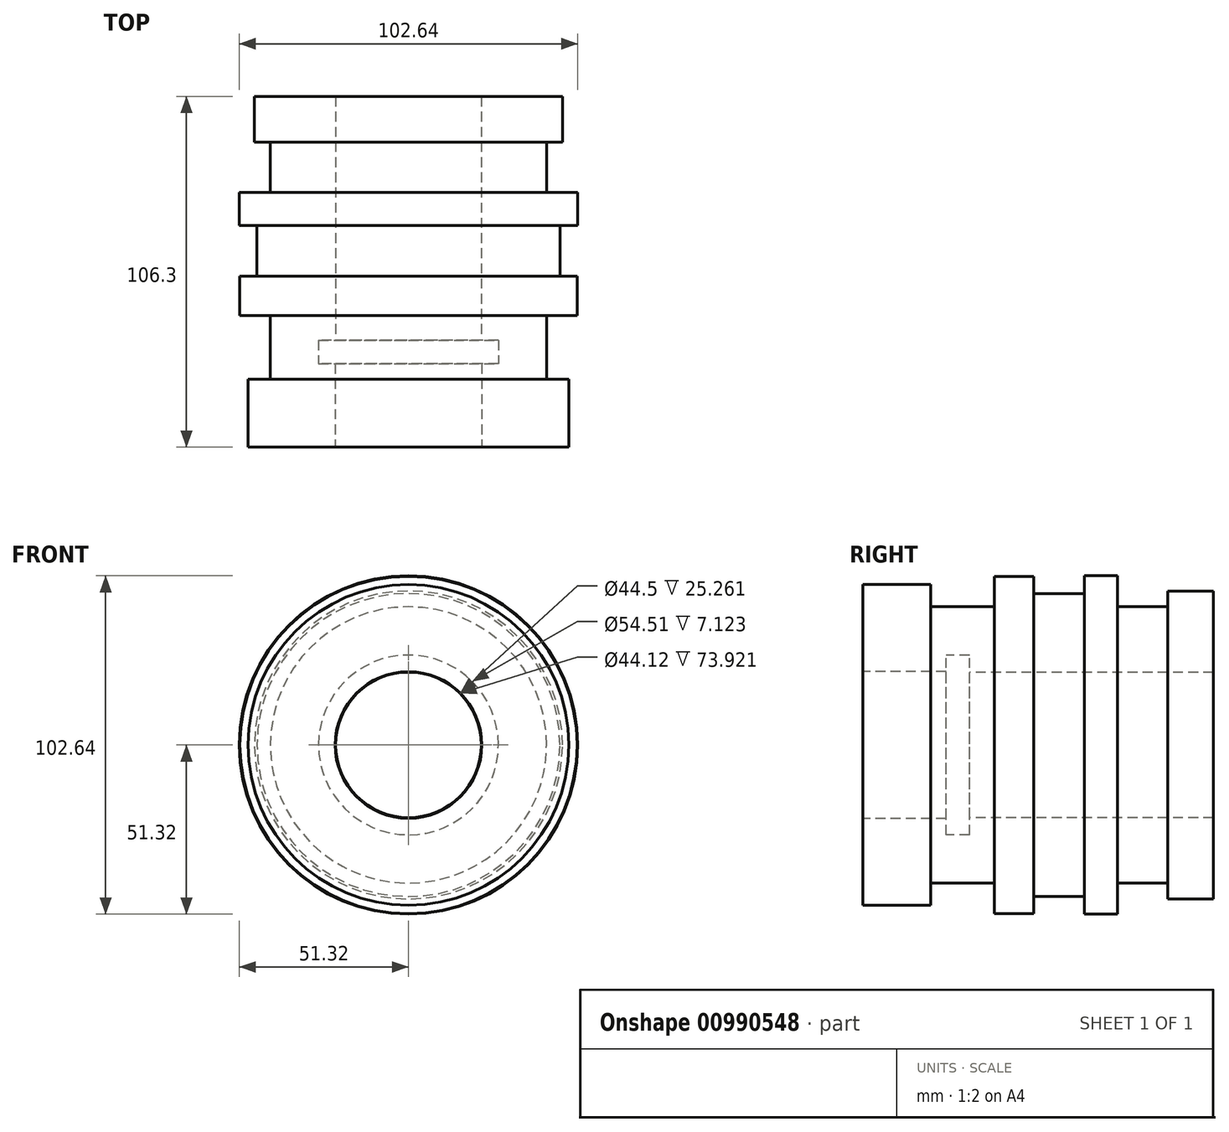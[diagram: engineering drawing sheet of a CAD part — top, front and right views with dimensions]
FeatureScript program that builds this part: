
annotation { "Feature Type Name" : "Feature", "Feature Type Description" : "" }
export const myFeature = defineFeature(function(context is Context, id is Id, definition is map)
    precondition{}
    {
        {
            var Q0;
            Q0=qCreatedBy(makeId("Right.planeOp"),FACE);
            var sketch = newSketch(context, id + "F0", { "sketchPlane" : qUnion([Q0])});
            skLineSegment(sketch, "E0", {"start": v(0, 0) * mm, "end": v(113.43, 0) * mm, "construction": true});
            skLineSegment(sketch, "E1", {"start": v(0, 22.25) * mm, "end": v(25.26, 22.25) * mm});
            skLineSegment(sketch, "E2", {"start": v(25.26, 22.25) * mm, "end": v(25.26, 27.26) * mm});
            skLineSegment(sketch, "E3", {"start": v(25.26, 27.26) * mm, "end": v(32.38, 27.26) * mm});
            skLineSegment(sketch, "E4", {"start": v(32.38, 27.26) * mm, "end": v(32.38, 22.06) * mm});
            skLineSegment(sketch, "E5", {"start": v(32.38, 22.06) * mm, "end": v(106.3, 22.06) * mm});
            skLineSegment(sketch, "E6", {"start": v(106.3, 22.06) * mm, "end": v(106.3, 46.7) * mm});
            skLineSegment(sketch, "E7", {"start": v(106.3, 46.7) * mm, "end": v(92.44, 46.7) * mm});
            skLineSegment(sketch, "E8", {"start": v(92.44, 46.7) * mm, "end": v(92.44, 41.89) * mm});
            skLineSegment(sketch, "E9", {"start": v(92.44, 41.89) * mm, "end": v(77.24, 41.89) * mm});
            skLineSegment(sketch, "E10", {"start": v(77.24, 41.89) * mm, "end": v(77.24, 51.32) * mm});
            skLineSegment(sketch, "E11", {"start": v(77.24, 51.32) * mm, "end": v(67.23, 51.32) * mm});
            skLineSegment(sketch, "E12", {"start": v(67.23, 51.32) * mm, "end": v(67.23, 45.93) * mm});
            skLineSegment(sketch, "E13", {"start": v(67.23, 45.93) * mm, "end": v(51.83, 45.93) * mm});
            skLineSegment(sketch, "E14", {"start": v(51.83, 45.93) * mm, "end": v(51.83, 51.13) * mm});
            skLineSegment(sketch, "E15", {"start": v(51.83, 51.13) * mm, "end": v(39.9, 51.13) * mm});
            skLineSegment(sketch, "E16", {"start": v(39.9, 51.13) * mm, "end": v(39.9, 41.89) * mm});
            skLineSegment(sketch, "E17", {"start": v(39.9, 41.89) * mm, "end": v(20.64, 41.89) * mm});
            skLineSegment(sketch, "E18", {"start": v(20.64, 41.89) * mm, "end": v(20.64, 48.63) * mm});
            skLineSegment(sketch, "E19", {"start": v(20.64, 48.63) * mm, "end": v(0, 48.63) * mm});
            skLineSegment(sketch, "E20", {"start": v(0, 48.63) * mm, "end": v(0, 22.25) * mm});
            skSolve(sketch);
        }
        {
            var Q0;
            Q0 = qSketchRegion(id + "F0", true);
            var Q1;
            Q1=sQuery(id+"F0.wireOp",EDGE,"E0");
            revolve(context, id + "F1", {"surfaceOperationType" : NewSurfaceOperationType.NEW, "entities" : qUnion([Q0]), "axis" : qUnion([Q1]), "revolveType" : RevolveType.FULL});
        }
    });
